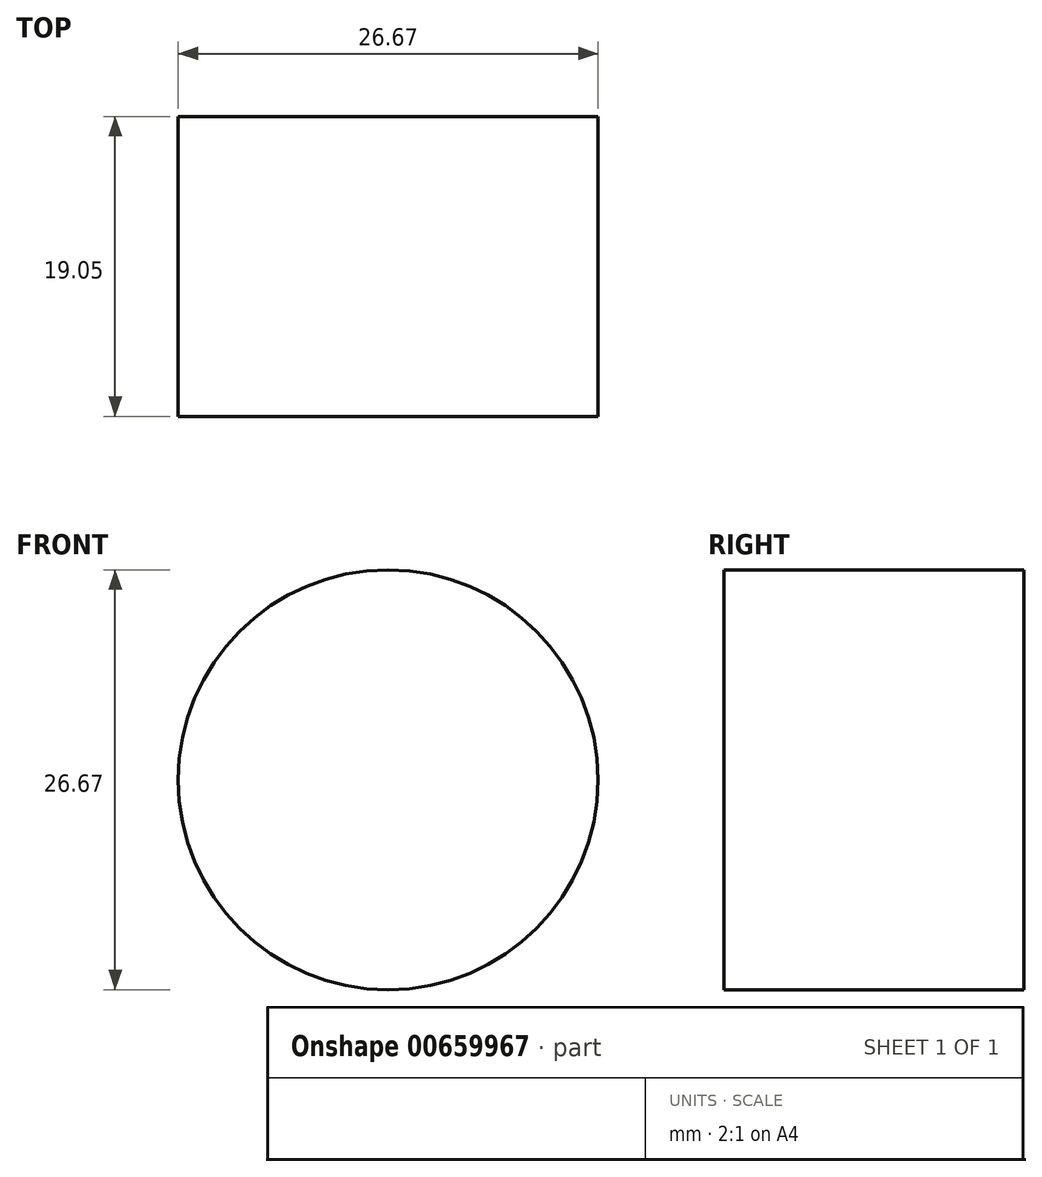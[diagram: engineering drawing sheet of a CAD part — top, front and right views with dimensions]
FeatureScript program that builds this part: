
annotation { "Feature Type Name" : "Feature", "Feature Type Description" : "" }
export const myFeature = defineFeature(function(context is Context, id is Id, definition is map)
    precondition{}
    {
        {
            var Q0;
            Q0=qCreatedBy(makeId("Front.planeOp"),FACE);
            var sketch = newSketch(context, id + "F0", { "sketchPlane" : qUnion([Q0])});
            skCircle(sketch, "E0", {"center": v(-12.12, -14.5) * mm, "radius": 13.33 * mm});
            skLineSegment(sketch, "E1", {"start": v(-19.7, -29.91) * mm, "end": v(-12.18, -29.91) * mm});
            skFitSpline(sketch, "E2", {"points": [v(-25.8, -59.84) * mm, v(-26.18, -59.78) * mm, v(-38.19, -53.84) * mm, v(-52.45, -38.51) * mm, v(-57.51, -24.56) * mm, v(-59.02, -15.14) * mm, v(-56.45, 0) * mm, v(-47.33, 14.14) * mm, v(-36.93, 21.2) * mm, v(-25.11, 24.54) * mm, v(-11.89, 23.51) * mm, v(0, 16.96) * mm, v(7.76, 7.2) * mm, v(10.46, -8.72) * mm, v(6.1, -20.28) * mm, v(-2.25, -27.99) * mm, v(-19.87, -29.97) * mm, v(-19.7, -29.91) * mm, v(-25.8, -59.84) * mm]});
            skFitSpline(sketch, "E3", {"points": [v(-21.33, -59.77) * mm, v(-27.77, -58.95) * mm, v(-30.05, -57.94) * mm], "startDerivative": vector(-9.8, 1.15) * mm, "endDerivative": vector(-4.94, 2.75) * mm});
            skFitSpline(sketch, "E4", {"points": [v(-21.33, -59.77) * mm, v(112.72, -53.86) * mm, v(222.7, -59.8) * mm, v(222.7, -29.95) * mm, v(112.72, -36.35) * mm, v(-19.87, -29.97) * mm], "startDerivative": vector(557, 74.4) * mm, "endDerivative": vector(-541.17, 79.73) * mm});
            skLineSegment(sketch, "E5", {"start": v(-19.7, -29.91) * mm, "end": v(-19.87, -29.97) * mm});
            skSolve(sketch);
        }
        {
            var Q0;
            Q0=qSketchRegion(id+"F0",true);
            extrude(context, id + "F1", {"entities" : qUnion([Q0]), "depth" : 19.05 * mm, "offsetDistance" : 25.4 * mm});
        }
    });
